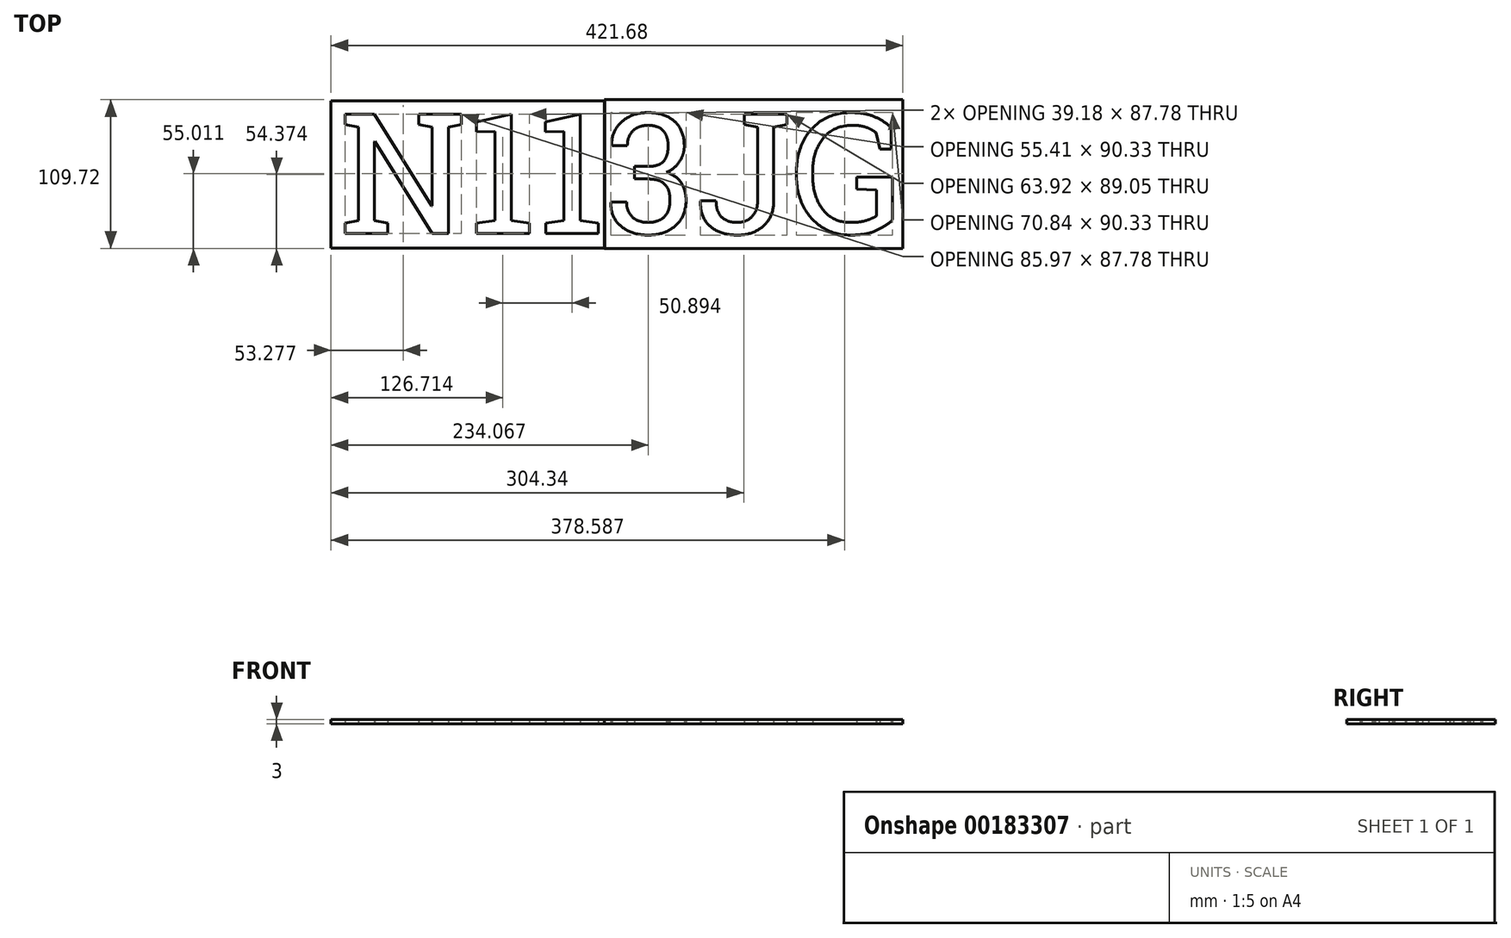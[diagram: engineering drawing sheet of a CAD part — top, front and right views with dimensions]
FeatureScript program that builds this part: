
annotation { "Feature Type Name" : "Feature", "Feature Type Description" : "" }
export const myFeature = defineFeature(function(context is Context, id is Id, definition is map)
    precondition{}
    {
        {
            var Q0;
            Q0=qCreatedBy(makeId("Top.planeOp"),FACE);
            var sketch = newSketch(context, id + "F0", { "sketchPlane" : qUnion([Q0])});
            skText(sketch, "E0", { "text": "N113JG\n\n", "fontName": "RobotoSlab-Regular.ttf"});
            const initialGuessF0  = {"E0": [0, 0, 1, 0, 0.0889]};
            skSetInitialGuess(sketch, initialGuessF0);
            skSolve(sketch);
        }
        {
            var Q0;
            Q0 = qSketchRegion(id + "F0", true);
            extrude(context, id + "F1", {"entities" : qUnion([Q0]), "depth" : 3 * mm, "offsetDistance" : 25 * mm});
        }
        {
            var Q0;
            Q0=qCreatedBy(makeId("Top.planeOp"),FACE);
            var sketch = newSketch(context, id + "F2", { "sketchPlane" : qUnion([Q0])});
            skLineSegment(sketch, "E1.bottom", {"start": v(-6.01, 97.78) * mm, "end": v(195.86, 97.78) * mm});
            skLineSegment(sketch, "E1.top", {"start": v(-6.01, -10.74) * mm, "end": v(195.86, -10.74) * mm});
            skLineSegment(sketch, "E1.left", {"start": v(-6.01, 97.78) * mm, "end": v(-6.01, -10.74) * mm});
            skLineSegment(sketch, "E1.right", {"start": v(195.86, 97.78) * mm, "end": v(195.86, -10.74) * mm});
            skSolve(sketch);
        }
        {
            var Q0;
            Q0 = qSketchRegion(id + "F2", true);
            extrude(context, id + "F3", {"entities" : qUnion([Q0]), "depth" : 3 * mm, "offsetDistance" : 25 * mm});
        }
        {
            var Q0;
            Q0=qCreatedBy(makeId("Top.planeOp"),FACE);
            var sketch = newSketch(context, id + "F4", { "sketchPlane" : qUnion([Q0])});
            skLineSegment(sketch, "E2.bottom", {"start": v(195.55, 98.6) * mm, "end": v(415.67, 98.6) * mm});
            skLineSegment(sketch, "E2.top", {"start": v(195.55, -11.12) * mm, "end": v(415.67, -11.12) * mm});
            skLineSegment(sketch, "E2.left", {"start": v(195.55, 98.6) * mm, "end": v(195.55, -11.12) * mm});
            skLineSegment(sketch, "E2.right", {"start": v(415.67, 98.6) * mm, "end": v(415.67, -11.12) * mm});
            skSolve(sketch);
        }
        {
            var Q0;
            Q0 = qSketchRegion(id + "F4", true);
            extrude(context, id + "F5", {"entities" : qUnion([Q0]), "depth" : 3 * mm, "offsetDistance" : 25 * mm});
        }
        {
            var Q0;
            Q0=makeQuery(id+"F1.opExtrude","SWEPT_BODY",BODY,{"disambiguationData":[OSD([sQuery(id+"F0.wireOp",EDGE,"E0.sketch_text.stroke-0"),sQuery(id+"F0.wireOp",EDGE,"E0.sketch_text.stroke-1"),sQuery(id+"F0.wireOp",EDGE,"E0.sketch_text.stroke-2"),sQuery(id+"F0.wireOp",EDGE,"E0.sketch_text.stroke-3"),sQuery(id+"F0.wireOp",EDGE,"E0.sketch_text.stroke-4"),sQuery(id+"F0.wireOp",EDGE,"E0.sketch_text.stroke-5"),sQuery(id+"F0.wireOp",EDGE,"E0.sketch_text.stroke-6"),sQuery(id+"F0.wireOp",EDGE,"E0.sketch_text.stroke-7"),sQuery(id+"F0.wireOp",EDGE,"E0.sketch_text.stroke-8"),sQuery(id+"F0.wireOp",EDGE,"E0.sketch_text.stroke-9"),sQuery(id+"F0.wireOp",EDGE,"E0.sketch_text.stroke-10"),sQuery(id+"F0.wireOp",EDGE,"E0.sketch_text.stroke-11"),sQuery(id+"F0.wireOp",EDGE,"E0.sketch_text.stroke-12"),sQuery(id+"F0.wireOp",EDGE,"E0.sketch_text.stroke-13"),sQuery(id+"F0.wireOp",EDGE,"E0.sketch_text.stroke-14"),sQuery(id+"F0.wireOp",EDGE,"E0.sketch_text.stroke-15"),sQuery(id+"F0.wireOp",EDGE,"E0.sketch_text.stroke-16"),sQuery(id+"F0.wireOp",EDGE,"E0.sketch_text.stroke-17"),sQuery(id+"F0.wireOp",EDGE,"E0.sketch_text.stroke-18"),sQuery(id+"F0.wireOp",EDGE,"E0.sketch_text.stroke-19"),sQuery(id+"F0.wireOp",EDGE,"E0.sketch_text.stroke-20"),sQuery(id+"F0.wireOp",EDGE,"E0.sketch_text.stroke-21"),sQuery(id+"F0.wireOp",EDGE,"E0.sketch_text.stroke-22"),sQuery(id+"F0.wireOp",EDGE,"E0.sketch_text.stroke-23")])]});
            var Q1;
            Q1=makeQuery(id+"F1.opExtrude","SWEPT_BODY",BODY,{"disambiguationData":[OSD([sQuery(id+"F0.wireOp",EDGE,"E0.sketch_text.stroke-24"),sQuery(id+"F0.wireOp",EDGE,"E0.sketch_text.stroke-25"),sQuery(id+"F0.wireOp",EDGE,"E0.sketch_text.stroke-26"),sQuery(id+"F0.wireOp",EDGE,"E0.sketch_text.stroke-27"),sQuery(id+"F0.wireOp",EDGE,"E0.sketch_text.stroke-28"),sQuery(id+"F0.wireOp",EDGE,"E0.sketch_text.stroke-29"),sQuery(id+"F0.wireOp",EDGE,"E0.sketch_text.stroke-30"),sQuery(id+"F0.wireOp",EDGE,"E0.sketch_text.stroke-31"),sQuery(id+"F0.wireOp",EDGE,"E0.sketch_text.stroke-32"),sQuery(id+"F0.wireOp",EDGE,"E0.sketch_text.stroke-33")])]});
            var Q2;
            Q2=makeQuery(id+"F1.opExtrude","SWEPT_BODY",BODY,{"disambiguationData":[OSD([sQuery(id+"F0.wireOp",EDGE,"E0.sketch_text.stroke-34"),sQuery(id+"F0.wireOp",EDGE,"E0.sketch_text.stroke-35"),sQuery(id+"F0.wireOp",EDGE,"E0.sketch_text.stroke-36"),sQuery(id+"F0.wireOp",EDGE,"E0.sketch_text.stroke-37"),sQuery(id+"F0.wireOp",EDGE,"E0.sketch_text.stroke-38"),sQuery(id+"F0.wireOp",EDGE,"E0.sketch_text.stroke-39"),sQuery(id+"F0.wireOp",EDGE,"E0.sketch_text.stroke-40"),sQuery(id+"F0.wireOp",EDGE,"E0.sketch_text.stroke-41"),sQuery(id+"F0.wireOp",EDGE,"E0.sketch_text.stroke-42"),sQuery(id+"F0.wireOp",EDGE,"E0.sketch_text.stroke-43")])]});
            var Q3;
            Q3=makeQuery(id+"F1.opExtrude","SWEPT_BODY",BODY,{"disambiguationData":[OSD([sQuery(id+"F0.wireOp",EDGE,"E0.sketch_text.stroke-44"),sQuery(id+"F0.wireOp",EDGE,"E0.sketch_text.stroke-45"),sQuery(id+"F0.wireOp",EDGE,"E0.sketch_text.stroke-46"),sQuery(id+"F0.wireOp",EDGE,"E0.sketch_text.stroke-47"),sQuery(id+"F0.wireOp",EDGE,"E0.sketch_text.stroke-48"),sQuery(id+"F0.wireOp",EDGE,"E0.sketch_text.stroke-49"),sQuery(id+"F0.wireOp",EDGE,"E0.sketch_text.stroke-50"),sQuery(id+"F0.wireOp",EDGE,"E0.sketch_text.stroke-51"),sQuery(id+"F0.wireOp",EDGE,"E0.sketch_text.stroke-52"),sQuery(id+"F0.wireOp",EDGE,"E0.sketch_text.stroke-53"),sQuery(id+"F0.wireOp",EDGE,"E0.sketch_text.stroke-54"),sQuery(id+"F0.wireOp",EDGE,"E0.sketch_text.stroke-55"),sQuery(id+"F0.wireOp",EDGE,"E0.sketch_text.stroke-56"),sQuery(id+"F0.wireOp",EDGE,"E0.sketch_text.stroke-57"),sQuery(id+"F0.wireOp",EDGE,"E0.sketch_text.stroke-58"),sQuery(id+"F0.wireOp",EDGE,"E0.sketch_text.stroke-59"),sQuery(id+"F0.wireOp",EDGE,"E0.sketch_text.stroke-60"),sQuery(id+"F0.wireOp",EDGE,"E0.sketch_text.stroke-61"),sQuery(id+"F0.wireOp",EDGE,"E0.sketch_text.stroke-62"),sQuery(id+"F0.wireOp",EDGE,"E0.sketch_text.stroke-63"),sQuery(id+"F0.wireOp",EDGE,"E0.sketch_text.stroke-64"),sQuery(id+"F0.wireOp",EDGE,"E0.sketch_text.stroke-65"),sQuery(id+"F0.wireOp",EDGE,"E0.sketch_text.stroke-66"),sQuery(id+"F0.wireOp",EDGE,"E0.sketch_text.stroke-67"),sQuery(id+"F0.wireOp",EDGE,"E0.sketch_text.stroke-68"),sQuery(id+"F0.wireOp",EDGE,"E0.sketch_text.stroke-69"),sQuery(id+"F0.wireOp",EDGE,"E0.sketch_text.stroke-70"),sQuery(id+"F0.wireOp",EDGE,"E0.sketch_text.stroke-71"),sQuery(id+"F0.wireOp",EDGE,"E0.sketch_text.stroke-72"),sQuery(id+"F0.wireOp",EDGE,"E0.sketch_text.stroke-73"),sQuery(id+"F0.wireOp",EDGE,"E0.sketch_text.stroke-74")])]});
            var Q4;
            Q4=makeQuery(id+"F1.opExtrude","SWEPT_BODY",BODY,{"disambiguationData":[OSD([sQuery(id+"F0.wireOp",EDGE,"E0.sketch_text.stroke-75"),sQuery(id+"F0.wireOp",EDGE,"E0.sketch_text.stroke-76"),sQuery(id+"F0.wireOp",EDGE,"E0.sketch_text.stroke-77"),sQuery(id+"F0.wireOp",EDGE,"E0.sketch_text.stroke-78"),sQuery(id+"F0.wireOp",EDGE,"E0.sketch_text.stroke-79"),sQuery(id+"F0.wireOp",EDGE,"E0.sketch_text.stroke-80"),sQuery(id+"F0.wireOp",EDGE,"E0.sketch_text.stroke-81"),sQuery(id+"F0.wireOp",EDGE,"E0.sketch_text.stroke-82"),sQuery(id+"F0.wireOp",EDGE,"E0.sketch_text.stroke-83"),sQuery(id+"F0.wireOp",EDGE,"E0.sketch_text.stroke-84"),sQuery(id+"F0.wireOp",EDGE,"E0.sketch_text.stroke-85"),sQuery(id+"F0.wireOp",EDGE,"E0.sketch_text.stroke-86"),sQuery(id+"F0.wireOp",EDGE,"E0.sketch_text.stroke-87"),sQuery(id+"F0.wireOp",EDGE,"E0.sketch_text.stroke-88"),sQuery(id+"F0.wireOp",EDGE,"E0.sketch_text.stroke-89"),sQuery(id+"F0.wireOp",EDGE,"E0.sketch_text.stroke-90"),sQuery(id+"F0.wireOp",EDGE,"E0.sketch_text.stroke-91"),sQuery(id+"F0.wireOp",EDGE,"E0.sketch_text.stroke-92")])]});
            var Q5;
            Q5=makeQuery(id+"F1.opExtrude","SWEPT_BODY",BODY,{"disambiguationData":[OSD([sQuery(id+"F0.wireOp",EDGE,"E0.sketch_text.stroke-93"),sQuery(id+"F0.wireOp",EDGE,"E0.sketch_text.stroke-94"),sQuery(id+"F0.wireOp",EDGE,"E0.sketch_text.stroke-95"),sQuery(id+"F0.wireOp",EDGE,"E0.sketch_text.stroke-96"),sQuery(id+"F0.wireOp",EDGE,"E0.sketch_text.stroke-97"),sQuery(id+"F0.wireOp",EDGE,"E0.sketch_text.stroke-98"),sQuery(id+"F0.wireOp",EDGE,"E0.sketch_text.stroke-99"),sQuery(id+"F0.wireOp",EDGE,"E0.sketch_text.stroke-100"),sQuery(id+"F0.wireOp",EDGE,"E0.sketch_text.stroke-101"),sQuery(id+"F0.wireOp",EDGE,"E0.sketch_text.stroke-102"),sQuery(id+"F0.wireOp",EDGE,"E0.sketch_text.stroke-103"),sQuery(id+"F0.wireOp",EDGE,"E0.sketch_text.stroke-104"),sQuery(id+"F0.wireOp",EDGE,"E0.sketch_text.stroke-105"),sQuery(id+"F0.wireOp",EDGE,"E0.sketch_text.stroke-106"),sQuery(id+"F0.wireOp",EDGE,"E0.sketch_text.stroke-107"),sQuery(id+"F0.wireOp",EDGE,"E0.sketch_text.stroke-108"),sQuery(id+"F0.wireOp",EDGE,"E0.sketch_text.stroke-109"),sQuery(id+"F0.wireOp",EDGE,"E0.sketch_text.stroke-110"),sQuery(id+"F0.wireOp",EDGE,"E0.sketch_text.stroke-111"),sQuery(id+"F0.wireOp",EDGE,"E0.sketch_text.stroke-112"),sQuery(id+"F0.wireOp",EDGE,"E0.sketch_text.stroke-113"),sQuery(id+"F0.wireOp",EDGE,"E0.sketch_text.stroke-114"),sQuery(id+"F0.wireOp",EDGE,"E0.sketch_text.stroke-115"),sQuery(id+"F0.wireOp",EDGE,"E0.sketch_text.stroke-116"),sQuery(id+"F0.wireOp",EDGE,"E0.sketch_text.stroke-117"),sQuery(id+"F0.wireOp",EDGE,"E0.sketch_text.stroke-118")])]});
            var Q6;
            Q6=makeQuery(id+"F3.opExtrude","SWEPT_BODY",BODY,{"disambiguationData":[OSD([sQuery(id+"F2.wireOp",EDGE,"E1.bottom"),sQuery(id+"F2.wireOp",EDGE,"E1.top"),sQuery(id+"F2.wireOp",EDGE,"E1.left"),sQuery(id+"F2.wireOp",EDGE,"E1.right")])]});
            var Q7;
            Q7=makeQuery(id+"F5.opExtrude","SWEPT_BODY",BODY,{"disambiguationData":[OSD([sQuery(id+"F4.wireOp",EDGE,"E2.bottom"),sQuery(id+"F4.wireOp",EDGE,"E2.top"),sQuery(id+"F4.wireOp",EDGE,"E2.left"),sQuery(id+"F4.wireOp",EDGE,"E2.right")])]});
            booleanBodies(context, id + "F6", {"operationType" : BooleanOperationType.SUBTRACTION, "tools" : qUnion([Q0, Q1, Q2, Q3, Q4, Q5]), "targets" : qUnion([Q6, Q7])});
        }
    });
